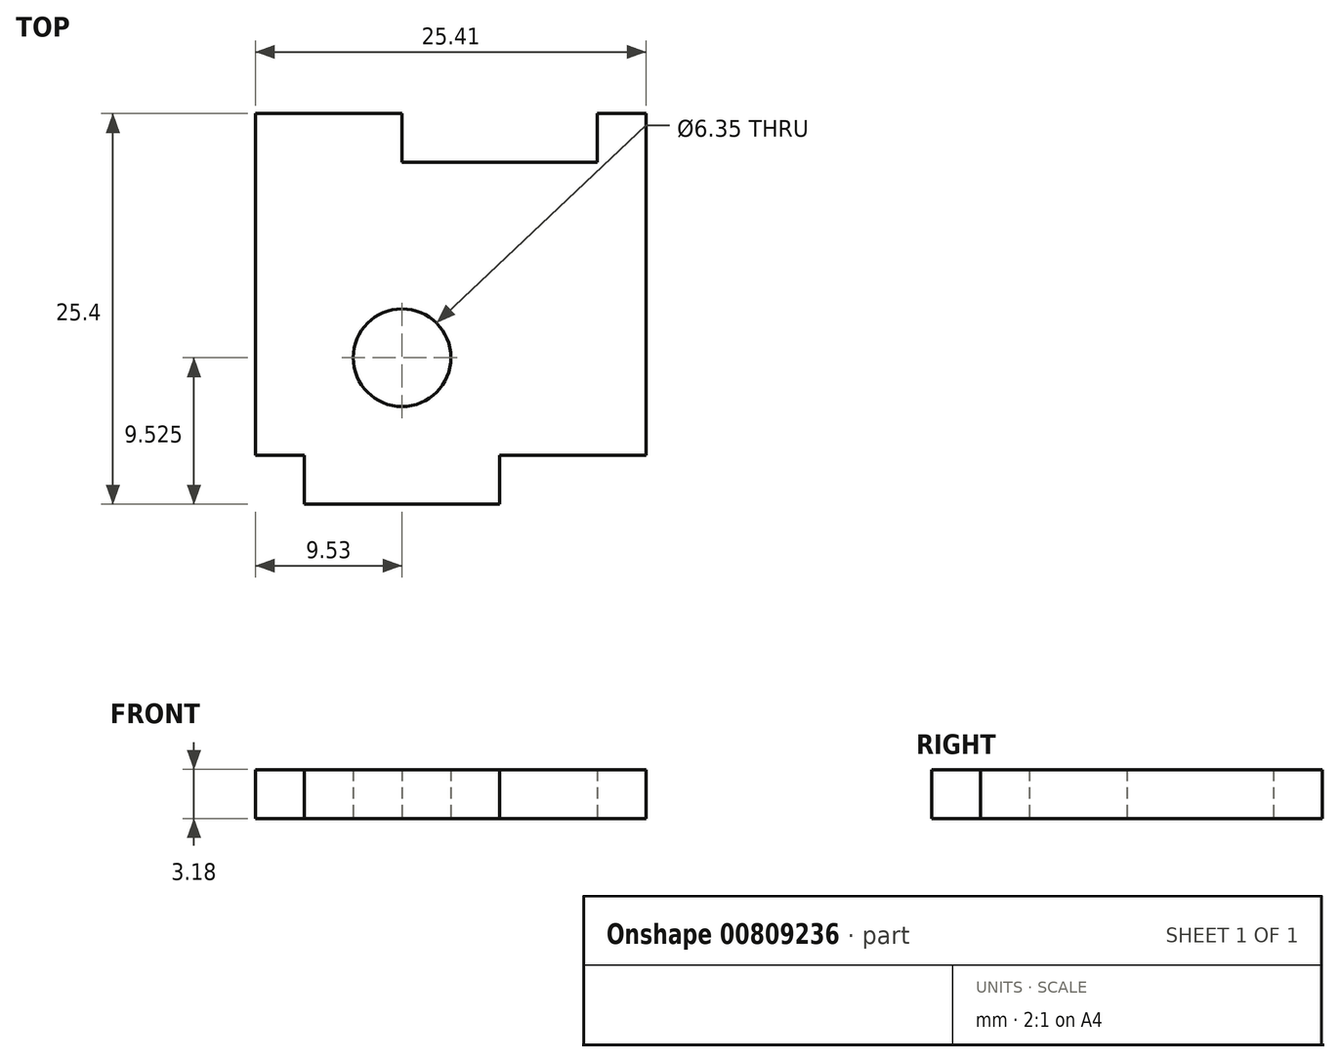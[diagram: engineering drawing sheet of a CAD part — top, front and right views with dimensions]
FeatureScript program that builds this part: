
annotation { "Feature Type Name" : "Feature", "Feature Type Description" : "" }
export const myFeature = defineFeature(function(context is Context, id is Id, definition is map)
    precondition{}
    {
        {
            var Q0;
            Q0=qCreatedBy(makeId("Top.planeOp"),FACE);
            var sketch = newSketch(context, id + "F0", { "sketchPlane" : qUnion([Q0])});
            skLineSegment(sketch, "E0.bottom", {"start": v(9.53, -9.53) * mm, "end": v(6.35, -9.53) * mm});
            skLineSegment(sketch, "E0.top", {"start": v(9.52, 9.52) * mm, "end": v(-9.52, 9.53) * mm});
            skLineSegment(sketch, "E0.left", {"start": v(9.52, -9.53) * mm, "end": v(9.52, 9.52) * mm});
            skLineSegment(sketch, "E0.right", {"start": v(-9.52, -9.52) * mm, "end": v(-9.52, 9.52) * mm});
            skPoint(sketch, "E0.middle", {"position": v(0, 0) * mm});
            skLineSegment(sketch, "E1.top", {"start": v(-6.35, -12.7) * mm, "end": v(6.35, -12.7) * mm});
            skLineSegment(sketch, "E1.left", {"start": v(-6.35, -9.52) * mm, "end": v(-6.35, -12.7) * mm});
            skLineSegment(sketch, "E1.right", {"start": v(6.35, -9.52) * mm, "end": v(6.35, -12.7) * mm});
            skPoint(sketch, "E2", {"position": v(0, -9.53) * mm});
            skCircle(sketch, "E3", {"center": v(0, -3.17) * mm, "radius": 3.18 * mm});
            skLineSegment(sketch, "E4.trimOffspring", {"start": v(-6.35, -9.53) * mm, "end": v(-9.53, -9.53) * mm});
            skLineSegment(sketch, "E5", {"start": v(6.35, -9.53) * mm, "end": v(-6.35, -9.53) * mm, "construction": true});
            skLineSegment(sketch, "E6.bottom", {"start": v(9.53, -9.53) * mm, "end": v(15.88, -9.53) * mm});
            skLineSegment(sketch, "E6.top", {"start": v(9.53, 9.52) * mm, "end": v(15.88, 9.52) * mm});
            skLineSegment(sketch, "E6.left", {"start": v(9.53, -9.52) * mm, "end": v(9.53, 9.52) * mm, "construction": true});
            skLineSegment(sketch, "E6.right", {"start": v(15.88, -9.53) * mm, "end": v(15.87, 9.53) * mm});
            skPoint(sketch, "E7", {"position": v(12.7, 9.52) * mm});
            skPoint(sketch, "E8", {"position": v(0, 9.53) * mm});
            skLineSegment(sketch, "E9.bottom", {"start": v(-9.52, 9.53) * mm, "end": v(0, 9.53) * mm});
            skLineSegment(sketch, "E9.top", {"start": v(-9.53, 12.7) * mm, "end": v(0, 12.7) * mm});
            skLineSegment(sketch, "E9.left", {"start": v(-9.52, 9.53) * mm, "end": v(-9.52, 12.7) * mm});
            skLineSegment(sketch, "E9.right", {"start": v(0, 9.53) * mm, "end": v(0, 12.7) * mm});
            skLineSegment(sketch, "E10.bottom", {"start": v(15.88, 9.52) * mm, "end": v(12.7, 9.52) * mm});
            skLineSegment(sketch, "E10.top", {"start": v(15.87, 12.7) * mm, "end": v(12.7, 12.7) * mm});
            skLineSegment(sketch, "E10.left", {"start": v(15.88, 9.52) * mm, "end": v(15.88, 12.7) * mm});
            skLineSegment(sketch, "E10.right", {"start": v(12.7, 9.52) * mm, "end": v(12.7, 12.7) * mm});
            skSolve(sketch);
        }
        {
            var Q0;
            {var subQ3=sQuery(id+"F0.wireOp",EDGE,"E0.left");Q0=makeQuery(id+"F0.imprint","IMPRINT",FACE,{"disambiguationData":[TD([[makeQuery(id+"F0.imprint","IMPRINT",EDGE,{"derivedFrom":subQ3}),-1.0]])]});}
            var Q1;
            Q1=makeQuery(id+"F0.imprint","IMPRINT",FACE,{"disambiguationData":[TD([[makeQuery(id+"F0.imprint","IMPRINT",EDGE,{"derivedFrom":sQuery(id+"F0.wireOp",EDGE,"E10.top")}),1.0]])]});
            var Q2;
            Q2=makeQuery(id+"F0.imprint","IMPRINT",FACE,{"disambiguationData":[TD([[makeQuery(id+"F0.imprint","IMPRINT",EDGE,{"derivedFrom":sQuery(id+"F0.wireOp",EDGE,"E9.top")}),-1.0]])]});
            var Q3;
            Q3=makeQuery(id+"F0.imprint","IMPRINT",FACE,{"disambiguationData":[TD([[makeQuery(id+"F0.imprint","IMPRINT",EDGE,{"derivedFrom":sQuery(id+"F0.wireOp",EDGE,"E0.bottom")}),-1.0]])]});
            extrude(context, id + "F1", {"entities" : qUnion([Q0, Q1, Q2, Q3]), "depth" : 3.17 * mm, "offsetDistance" : 25.4 * mm});
        }
    });
